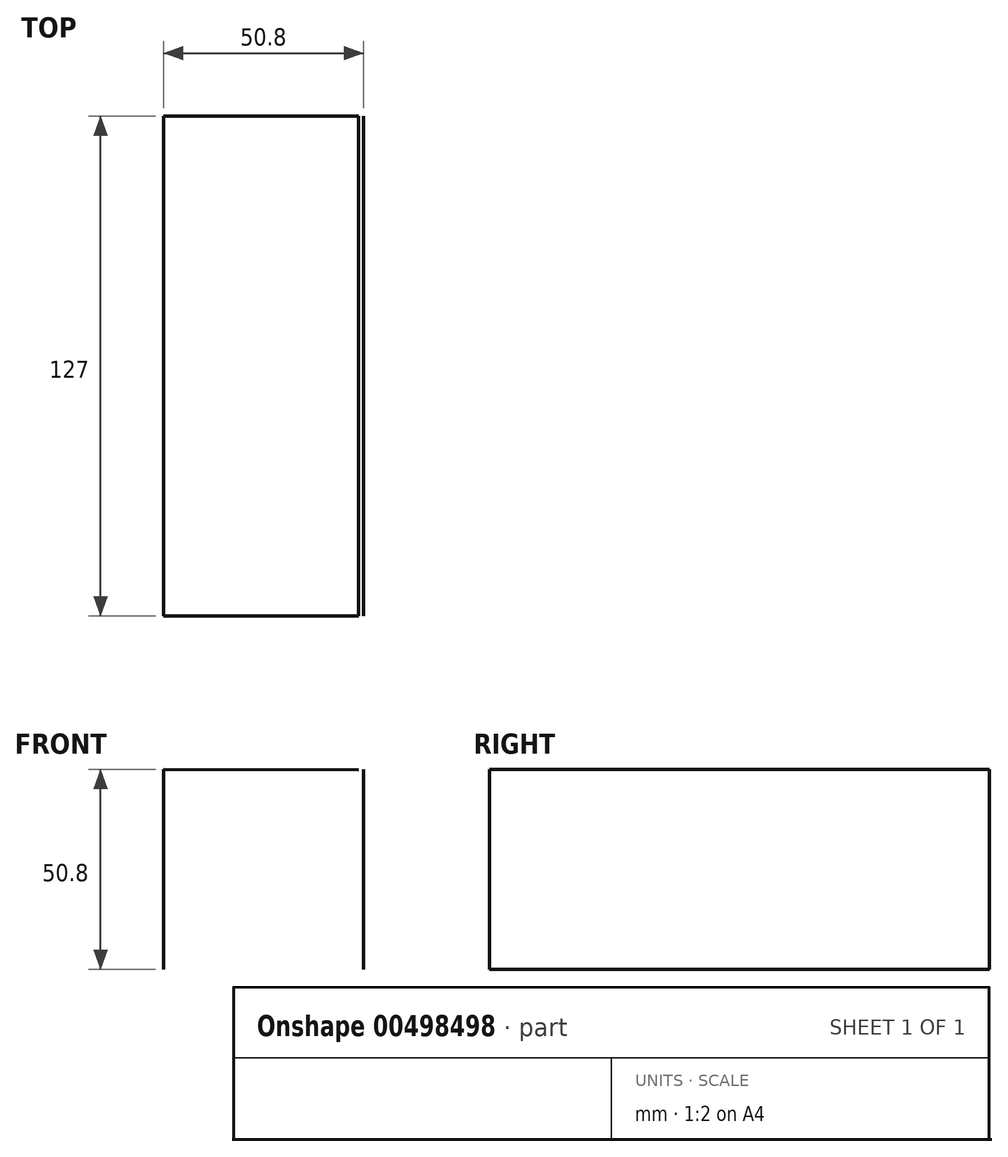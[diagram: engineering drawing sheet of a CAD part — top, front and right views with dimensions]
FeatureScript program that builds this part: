
annotation { "Feature Type Name" : "Feature", "Feature Type Description" : "" }
export const myFeature = defineFeature(function(context is Context, id is Id, definition is map)
    precondition{}
    {
        {
            var Q0;
            Q0=qCreatedBy(makeId("Front.planeOp"),FACE);
            var sketch = newSketch(context, id + "F0", { "sketchPlane" : qUnion([Q0])});
            skLineSegment(sketch, "E0.left", {"start": v(25.4, -25.4) * mm, "end": v(25.4, 25.4) * mm});
            skLineSegment(sketch, "E0.right", {"start": v(-25.4, -25.4) * mm, "end": v(-25.4, 25.4) * mm});
            skPoint(sketch, "E0.middle", {"position": v(0, 0) * mm});
            skLineSegment(sketch, "E1", {"start": v(24.08, 25.3) * mm, "end": v(-25.4, 25.4) * mm});
            skSolve(sketch);
        }
        {
            var Q0;
            Q0 = qSketchRegion(id + "FcMyK5HkFdklARP_0", true);
            var Q1;
            Q1=sQuery(id+"F0.wireOp",EDGE,"E0.left");
            var Q2;
            Q2=sQuery(id+"F0.wireOp",EDGE,"E0.right");
            var Q3;
            Q3=sQuery(id+"F0.wireOp",EDGE,"E1");
            var Q4;
            Q4 = qSketchRegion(id + "FcMyK5HkFdklARP_0", true);
            extrude(context, id + "F1", {"entities" : qUnion([Q0]), "bodyType" : ToolBodyType.SURFACE, "surfaceEntities" : qUnion([Q1, Q2, Q3, Q4]), "oppositeDirection" : true, "depth" : 127 * mm});
        }
    });
